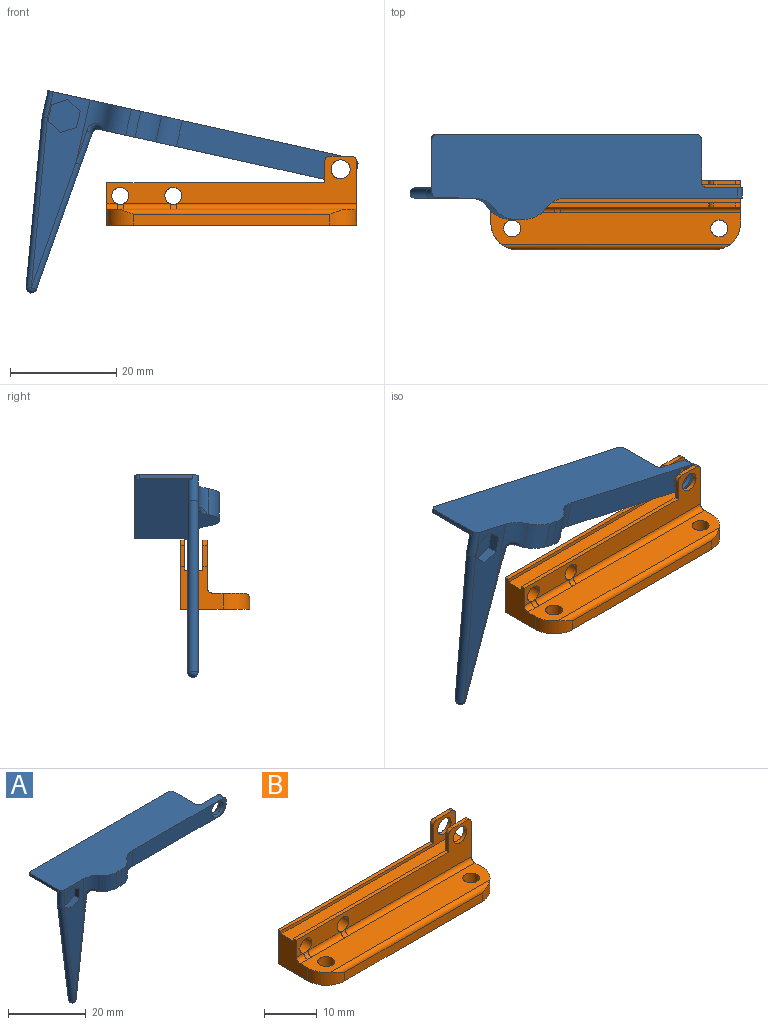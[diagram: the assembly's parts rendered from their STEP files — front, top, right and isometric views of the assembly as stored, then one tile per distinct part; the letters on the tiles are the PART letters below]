
ASSEMBLY  parts=2 mates=1
PART A: 38 faces, bbox 60.5x16.5x38.4 mm
  f0: plane 59x36.94mm, normal (0,1,0), area 332.8mm2, adj f3,f6,f7,f10,f12,f13,f14,f15
  f1: plane 36.94x7.1mm, normal (0,-1,0), area 133.6mm2, adj f3,f12,f13,f14,f15,f16,f17,f19
  f2: plane 34.1x5mm, normal (0,-1,0), area 152.3mm2, adj f3,f6,f7,f10,f18,f35,f37
  f3: plane 59x16mm, normal (0,0,1), area 676.8mm2, adj f0,f1,f2,f4,f10,f11,f18,f19
  f4: plane 10x0.82mm, normal (-1,0,0), area 8.2mm2, adj f3,f22,f26,f28
  f5: plane 6.38x0.8mm, normal (0.99,0,-0.12), area 0.1mm2, adj f9,f32,f34
  f6: plane 47.12x6.5mm, normal (0,0,-1), area 130.7mm2, adj f0,f2,f9,f11,f18,f19,f20,f21
  f7: plane 2x1.5mm, normal (1,0,0), area 3mm2, adj f0,f2,f10,f37
  f8: cylinder r=1.8mm len=3.6mm, axis (0,1,0), area 11.3mm2, adj f35,f36
  f9: cylinder r=1mm len=0.99mm, axis (0,1,0), area 0.4mm2, adj f5,f6,f30,f33
  f10: cylinder r=1mm len=2mm, axis (0,-1,0), area 3.1mm2, adj f0,f2,f3,f7
  f11: plane 5x1.8mm, normal (0,-1,0), area 9mm2, adj f3,f6,f20,f21
  f12: plane 2.75x2mm, normal (-0.5,0,-0.87), area 6.4mm2, adj f0,f1,f13,f17
  f13: plane 2.75x2mm, normal (0.5,0,-0.87), area 6.4mm2, adj f0,f1,f12,f14
  f14: plane 3.18x2mm, normal (1,0,0), area 6.4mm2, adj f0,f1,f13,f15
  f15: plane 2.75x2mm, normal (0.5,0,0.87), area 6.4mm2, adj f0,f1,f14,f16
  f16: plane 2.75x2mm, normal (-0.5,0,0.87), area 6.4mm2, adj f0,f1,f15,f17
  f17: plane 3.18x2mm, normal (-1,0,0), area 6.4mm2, adj f0,f1,f12,f16
  f18: cylinder r=5mm len=5mm, axis (0,0,-1), area 23.2mm2, adj f2,f3,f6,f21
  f19: cylinder r=5mm len=12.13mm, axis (0,0,1), area 23.5mm2, adj f1,f3,f6,f20,f33,f34
  f20: cylinder r=5mm len=5mm, axis (0,0,1), area 23.2mm2, adj f3,f6,f11,f19
  f21: cylinder r=5mm len=5mm, axis (0,0,-1), area 23.2mm2, adj f3,f6,f11,f18
  f22: plane 53x11mm, normal (0,0,-1), area 520mm2, adj f0,f4,f23,f24,f25,f26,f27,f28
  f23: plane 8x0.82mm, normal (1,0,0), area 6.6mm2, adj f3,f22,f25,f27
  f24: plane 50x0.82mm, normal (0,1,0), area 41.2mm2, adj f3,f22,f26,f27
  f25: cylinder r=1mm len=1mm, axis (0,0,1), area 1.3mm2, adj f0,f3,f22,f23
  f26: cylinder r=1mm len=1mm, axis (0,0,1), area 1.3mm2, adj f3,f4,f22,f24
  f27: cylinder r=1mm len=1mm, axis (0,0,1), area 1.3mm2, adj f3,f22,f23,f24
  f28: cylinder r=1mm len=4.94mm, axis (0,0,-1), area 14.2mm2, adj f0,f1,f3,f4,f22,f29
  f29: cylinder r=1mm len=32.12mm, axis (0.12,0,-0.99), area 101.3mm2, adj f0,f1,f28,f31
  f30: torus R=2mm, axis (0,-1,0), area 4.4mm2, adj f0,f6,f9,f32
  f31: sphere r=1mm, area 6mm2, adj f29,f32
  f32: cylinder r=1mm len=31.31mm, axis (0.12,0,0.99), area 88.6mm2, adj f0,f1,f5,f30,f31,f34
  f33: bspline ~3.23x2.79mm, area 4.4mm2, adj f6,f9,f19,f34
  f34: bspline ~6.5x1.79mm, area 10.5mm2, adj f5,f19,f32,f33
  f35: cone r=1.8mm half-angle=45deg, axis (0,-1,0), area 9.1mm2, adj f2,f8
  f36: cone r=2.3mm half-angle=45deg, axis (0,1,0), area 9.1mm2, adj f0,f8
  f37: cylinder r=2.5mm len=2.5mm, axis (0,-1,0), area 7.9mm2, adj f0,f2,f6,f7
PART B: 34 faces, bbox 47x13x13 mm
  f0: cylinder r=1mm len=1mm, axis (0,-1,0), area 1.3mm2, adj f2,f7,f15,f18
  f1: cylinder r=1mm len=1mm, axis (0,-1,0), area 1.3mm2, adj f3,f7,f16,f19
  f2: plane 4x0.8mm, normal (0,0,1), area 3.2mm2, adj f0,f15,f18,f21
  f3: plane 4x0.8mm, normal (0,0,1), area 3.2mm2, adj f1,f16,f19,f20
  f4: plane 4x0.8mm, normal (-1,0,0), area 3.2mm2, adj f5,f16,f19,f20
  f5: plane 41x0.8mm, normal (0,0,1), area 32.8mm2, adj f4,f10,f16,f19
  f6: cylinder r=1.8mm len=3.6mm, axis (0,1,0), area 9mm2, adj f16,f19
  f7: plane 12x8mm, normal (1,0,0), area 53.2mm2, adj f0,f1,f13,f15,f16,f17,f18,f19
  f8: plane 4x0.8mm, normal (-1,0,0), area 3.2mm2, adj f9,f15,f18,f21
  f9: plane 41x0.8mm, normal (0,0,1), area 32.8mm2, adj f8,f10,f15,f18
  f10: plane 8x8mm, normal (-1,0,0), area 46.8mm2, adj f5,f9,f13,f15,f16,f17,f18,f19
  f11: cylinder r=1.6mm len=5mm, axis (0,1,0), area 50.3mm2, adj f15,f16,f30
  f12: cylinder r=1.6mm len=5mm, axis (0,1,0), area 50.3mm2, adj f15,f16,f32
  f13: plane 47x13mm, normal (0,0,-1), area 584.2mm2, adj f7,f10,f16,f23,f24,f25,f26,f27
  f14: cylinder r=1.8mm len=3.6mm, axis (0,1,0), area 9mm2, adj f15,f18
  f15: plane 47x9mm, normal (0,-1,0), area 191.5mm2, adj f0,f2,f7,f8,f9,f10,f11,f12
  f16: plane 47x13mm, normal (0,1,0), area 379.3mm2, adj f1,f3,f4,f5,f6,f7,f10,f11
  f17: plane 47x3.4mm, normal (0,0,1), area 159.8mm2, adj f7,f10,f18,f19
  f18: plane 47x5.7mm, normal (0,1,0), area 52.3mm2, adj f0,f2,f7,f8,f9,f10,f14,f17
  f19: plane 47x5.7mm, normal (0,-1,0), area 52.3mm2, adj f1,f3,f4,f5,f6,f7,f10,f17
  f20: cylinder r=1mm len=1mm, axis (0,1,0), area 1.3mm2, adj f3,f4,f16,f19
  f21: cylinder r=1mm len=1mm, axis (0,1,0), area 1.3mm2, adj f2,f8,f15,f18
  f22: plane 47x6.01mm, normal (0,0,1), area 261.1mm2, adj f7,f10,f24,f25,f26,f27,f28,f29
  f23: plane 37x2mm, normal (0,-1,0), area 74mm2, adj f13,f24,f25,f28
  f24: cylinder r=5mm len=5mm, axis (0,0,1), area 22mm2, adj f10,f13,f22,f23,f28
  f25: cylinder r=5mm len=5mm, axis (0,0,-1), area 22mm2, adj f7,f13,f22,f23,f28
  f26: cylinder r=1.6mm len=3.2mm, axis (0,0,1), area 30.2mm2, adj f13,f22
  f27: cylinder r=1.6mm len=3.2mm, axis (0,0,1), area 30.2mm2, adj f13,f22
  f28: cylinder r=1mm len=43mm, axis (1,0,0), area 62.8mm2, adj f22,f23,f24,f25
  f29: cylinder r=1mm len=1.94mm, axis (1,0,0), area 3.1mm2, adj f10,f15,f22,f30
  f30: bspline ~1.88x1.21mm, area 1.7mm2, adj f11,f22,f29,f31
  f31: cylinder r=1mm len=8.89mm, axis (1,0,0), area 14mm2, adj f15,f22,f30,f32
  f32: bspline ~1.88x1.21mm, area 1.7mm2, adj f12,f22,f31,f33
  f33: cylinder r=1mm len=33.94mm, axis (1,0,0), area 53.3mm2, adj f7,f15,f22,f32
PLACE A rot(axis=(0,1,0),12.5deg) t=(-24.99,7.6,-12.91)mm
PLACE B t=(-25.65,7.4,-23.93)mm fixed
MATE revolute A.f8 <-> B.f6  axis (0,1,0) through (24.84,8.6,-21.43)mm
